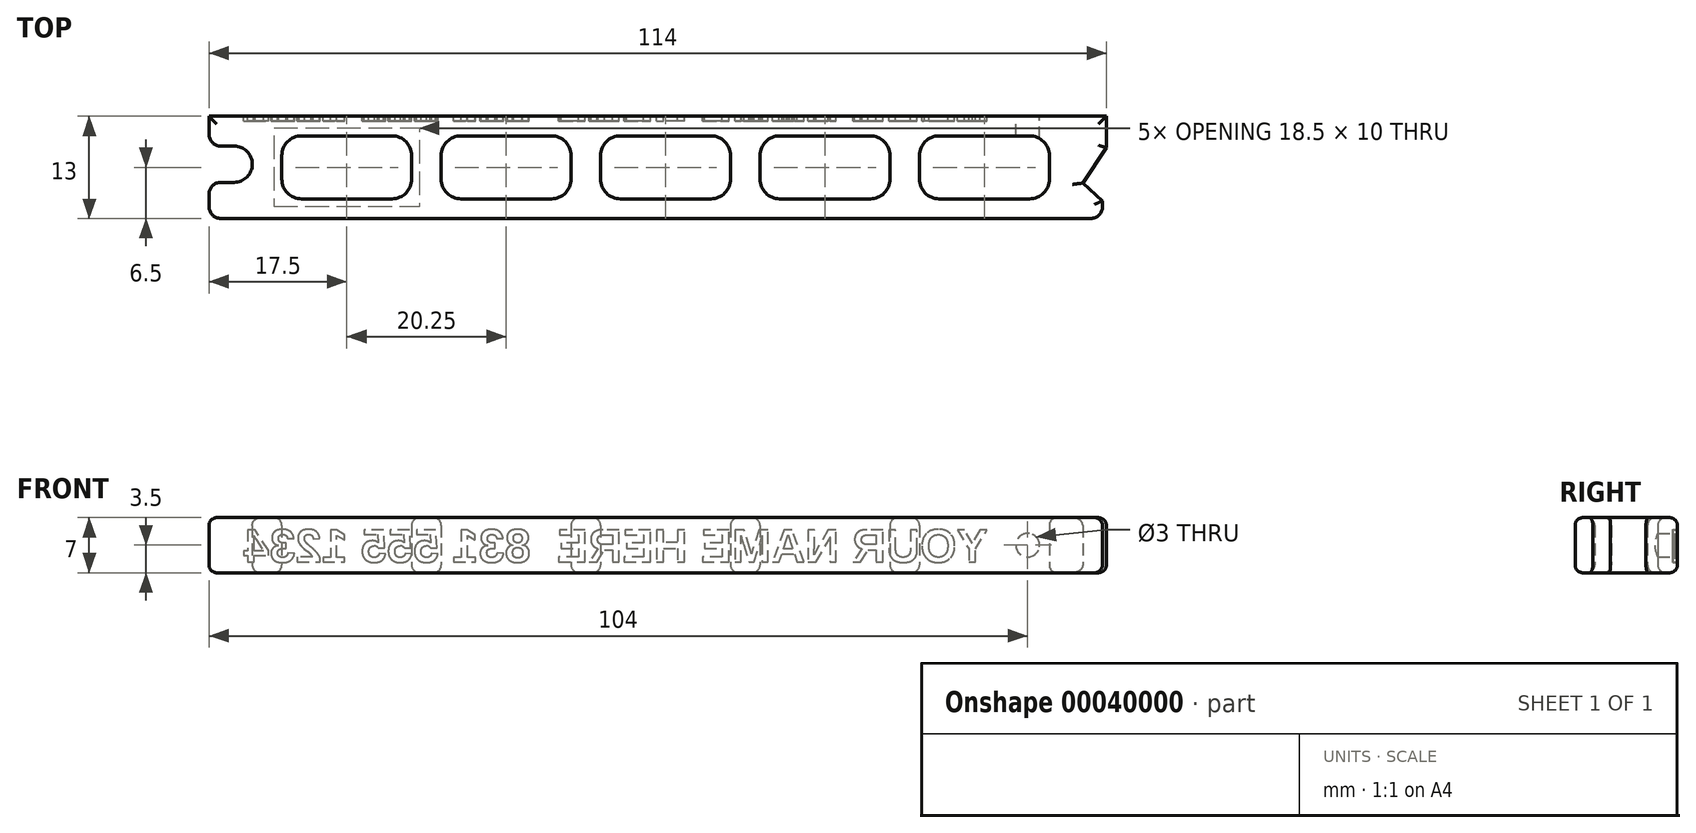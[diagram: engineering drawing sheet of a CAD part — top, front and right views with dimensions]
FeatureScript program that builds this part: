
annotation { "Feature Type Name" : "Feature", "Feature Type Description" : "" }
export const myFeature = defineFeature(function(context is Context, id is Id, definition is map)
    precondition{}
    {
        {
            var Q0;
            Q0=qCreatedBy(makeId("Top.planeOp"),FACE);
            var sketch = newSketch(context, id + "F0", { "sketchPlane" : qUnion([Q0])});
            skLineSegment(sketch, "E0.bottom", {"start": v(1.5, 0) * mm, "end": v(112, 0) * mm});
            skLineSegment(sketch, "E0.top", {"start": v(0, 13) * mm, "end": v(114, 13) * mm});
            skLineSegment(sketch, "E1", {"start": v(0, 13) * mm, "end": v(0, 10.7) * mm});
            skLineSegment(sketch, "E2.bottom", {"start": v(1.5, 4.6) * mm, "end": v(3.2, 4.6) * mm});
            skLineSegment(sketch, "E2.top", {"start": v(1.5, 9.2) * mm, "end": v(3.2, 9.2) * mm});
            skArc(sketch, "E3", {"start": v(3.2, 4.6) * mm, "mid": v(5.5, 6.9) * mm, "end": v(3.2, 9.2) * mm});
            skLineSegment(sketch, "E4.trimOffspring", {"start": v(0, 3.1) * mm, "end": v(0, 1.5) * mm});
            skLineSegment(sketch, "E5", {"start": v(0, 9.2) * mm, "end": v(0, 4.6) * mm, "construction": true});
            skLineSegment(sketch, "E6", {"start": v(0, 6.9) * mm, "end": v(3.2, 6.9) * mm, "construction": true});
            skLineSegment(sketch, "E7", {"start": v(114, 13) * mm, "end": v(114, 9) * mm});
            skPoint(sketch, "E8.visualSharp", {"position": v(0, 0) * mm});
            skArc(sketch, "E8.filletArc", {"start": v(0, 1.5) * mm, "mid": v(0.44, 0.44) * mm, "end": v(1.5, 0) * mm});
            skPoint(sketch, "E9.visualSharp", {"position": v(0, 4.6) * mm});
            skArc(sketch, "E9.filletArc", {"start": v(1.5, 4.6) * mm, "mid": v(0.44, 4.16) * mm, "end": v(0, 3.1) * mm});
            skPoint(sketch, "E10.visualSharp", {"position": v(0, 9.2) * mm});
            skArc(sketch, "E10.filletArc", {"start": v(0, 10.7) * mm, "mid": v(0.44, 9.64) * mm, "end": v(1.5, 9.2) * mm});
            skPoint(sketch, "E11.visualSharp", {"position": v(114, 4.5) * mm});
            skLineSegment(sketch, "E12", {"start": v(114, 4.5) * mm, "end": v(111, 4.5) * mm, "construction": true});
            skLineSegment(sketch, "E13", {"start": v(114, 9) * mm, "end": v(111, 4.5) * mm});
            skLineSegment(sketch, "E14", {"start": v(113.5, 2.25) * mm, "end": v(111, 4.5) * mm});
            skArc(sketch, "E15", {"start": v(112, 0) * mm, "mid": v(113.06, 0.44) * mm, "end": v(113.5, 1.5) * mm});
            skLineSegment(sketch, "E16", {"start": v(112, 1.5) * mm, "end": v(114.8, 1.5) * mm, "construction": true});
            skLineSegment(sketch, "E17", {"start": v(113.5, 2.25) * mm, "end": v(113.5, 1.5) * mm});
            skSolve(sketch);
        }
        {
            var Q0;
            Q0=makeQuery(id+"F0.imprint","IMPRINT",FACE,{"disambiguationData":[TD([[makeQuery(id+"F0.imprint","IMPRINT",EDGE,{"derivedFrom":sQuery(id+"F0.wireOp",EDGE,"E0.bottom")}),1.0]])]});
            extrude(context, id + "F1", {"entities" : qUnion([Q0]), "depth" : 7 * mm});
        }
        {
            var Q0;
            Q0=makeQuery(id+"F1.opExtrude","CAP_FACE",FACE,{"disambiguationData":[OSD([sQuery(id+"F0.wireOp",EDGE,"E0.bottom"),sQuery(id+"F0.wireOp",EDGE,"E0.top"),sQuery(id+"F0.wireOp",EDGE,"E1"),sQuery(id+"F0.wireOp",EDGE,"E2.bottom"),sQuery(id+"F0.wireOp",EDGE,"E2.top"),sQuery(id+"F0.wireOp",EDGE,"E3"),sQuery(id+"F0.wireOp",EDGE,"E4.trimOffspring"),sQuery(id+"F0.wireOp",EDGE,"E7"),sQuery(id+"F0.wireOp",EDGE,"c30ca287-96d4-4dfe-8688-3bdeec023004"),sQuery(id+"F0.wireOp",EDGE,"f645941c-dc99-4dda-a8e2-c4b280260802"),sQuery(id+"F0.wireOp",EDGE,"a89c6d0d-95b4-4aa5-8d05-a083aa38cfd4")])],"isStart":true});
            var sketch = newSketch(context, id + "F2", { "sketchPlane" : qUnion([Q0])});
            skLineSegment(sketch, "E18.bottom", {"start": v(104.25, -2.5) * mm, "end": v(92.75, -2.5) * mm});
            skLineSegment(sketch, "E18.top", {"start": v(104.25, -10.5) * mm, "end": v(92.75, -10.5) * mm});
            skLineSegment(sketch, "E18.left", {"start": v(106.75, -5) * mm, "end": v(106.75, -8) * mm});
            skLineSegment(sketch, "E18.right", {"start": v(90.25, -5) * mm, "end": v(90.25, -8) * mm});
            skLineSegment(sketch, "E19", {"start": v(106.75, -10.5) * mm, "end": v(106.75, -13) * mm, "construction": true});
            skLineSegment(sketch, "E20", {"start": v(106.75, -2.5) * mm, "end": v(106.75, 0) * mm, "construction": true});
            skPoint(sketch, "E21.visualSharp", {"position": v(90.25, -10.5) * mm});
            skArc(sketch, "E21.filletArc", {"start": v(90.25, -8) * mm, "mid": v(90.98, -9.77) * mm, "end": v(92.75, -10.5) * mm});
            skPoint(sketch, "E22.visualSharp", {"position": v(90.25, -2.5) * mm});
            skArc(sketch, "E22.filletArc", {"start": v(92.75, -2.5) * mm, "mid": v(90.98, -3.23) * mm, "end": v(90.25, -5) * mm});
            skPoint(sketch, "E23.visualSharp", {"position": v(106.75, -2.5) * mm});
            skArc(sketch, "E23.filletArc", {"start": v(106.75, -5) * mm, "mid": v(106.02, -3.23) * mm, "end": v(104.25, -2.5) * mm});
            skPoint(sketch, "E24.visualSharp", {"position": v(106.75, -10.5) * mm});
            skArc(sketch, "E24.filletArc", {"start": v(104.25, -10.5) * mm, "mid": v(106.02, -9.77) * mm, "end": v(106.75, -8) * mm});
            skLineSegment(sketch, "E25.1.0.0", {"start": v(84, -2.5) * mm, "end": v(72.5, -2.5) * mm});
            skPoint(sketch, "E25.1.0.1", {"position": v(86.5, -2.5) * mm});
            skLineSegment(sketch, "E25.1.0.2", {"start": v(84, -10.5) * mm, "end": v(72.5, -10.5) * mm});
            skPoint(sketch, "E25.1.0.3", {"position": v(86.5, -10.5) * mm});
            skLineSegment(sketch, "E25.1.0.4", {"start": v(70, -5) * mm, "end": v(70, -8) * mm});
            skLineSegment(sketch, "E25.1.0.5", {"start": v(86.5, -5) * mm, "end": v(86.5, -8) * mm});
            skPoint(sketch, "E25.1.0.6", {"position": v(70, -2.5) * mm});
            skPoint(sketch, "E25.1.0.7", {"position": v(70, -10.5) * mm});
            skArc(sketch, "E25.1.0.8", {"start": v(72.5, -2.5) * mm, "mid": v(70.73, -3.23) * mm, "end": v(70, -5) * mm});
            skArc(sketch, "E25.1.0.9", {"start": v(70, -8) * mm, "mid": v(70.73, -9.77) * mm, "end": v(72.5, -10.5) * mm});
            skArc(sketch, "E25.1.0.10", {"start": v(86.5, -5) * mm, "mid": v(85.77, -3.23) * mm, "end": v(84, -2.5) * mm});
            skArc(sketch, "E25.1.0.11", {"start": v(84, -10.5) * mm, "mid": v(85.77, -9.77) * mm, "end": v(86.5, -8) * mm});
            skLineSegment(sketch, "E25.2.0.0", {"start": v(63.75, -2.5) * mm, "end": v(52.25, -2.5) * mm});
            skPoint(sketch, "E25.2.0.1", {"position": v(66.25, -2.5) * mm});
            skLineSegment(sketch, "E25.2.0.2", {"start": v(63.75, -10.5) * mm, "end": v(52.25, -10.5) * mm});
            skPoint(sketch, "E25.2.0.3", {"position": v(66.25, -10.5) * mm});
            skLineSegment(sketch, "E25.2.0.4", {"start": v(49.75, -5) * mm, "end": v(49.75, -8) * mm});
            skLineSegment(sketch, "E25.2.0.5", {"start": v(66.25, -5) * mm, "end": v(66.25, -8) * mm});
            skPoint(sketch, "E25.2.0.6", {"position": v(49.75, -2.5) * mm});
            skPoint(sketch, "E25.2.0.7", {"position": v(49.75, -10.5) * mm});
            skArc(sketch, "E25.2.0.8", {"start": v(52.25, -2.5) * mm, "mid": v(50.48, -3.23) * mm, "end": v(49.75, -5) * mm});
            skArc(sketch, "E25.2.0.9", {"start": v(49.75, -8) * mm, "mid": v(50.48, -9.77) * mm, "end": v(52.25, -10.5) * mm});
            skArc(sketch, "E25.2.0.10", {"start": v(66.25, -5) * mm, "mid": v(65.52, -3.23) * mm, "end": v(63.75, -2.5) * mm});
            skArc(sketch, "E25.2.0.11", {"start": v(63.75, -10.5) * mm, "mid": v(65.52, -9.77) * mm, "end": v(66.25, -8) * mm});
            skLineSegment(sketch, "E25.3.0.0", {"start": v(43.5, -2.5) * mm, "end": v(32, -2.5) * mm});
            skPoint(sketch, "E25.3.0.1", {"position": v(46, -2.5) * mm});
            skLineSegment(sketch, "E25.3.0.2", {"start": v(43.5, -10.5) * mm, "end": v(32, -10.5) * mm});
            skPoint(sketch, "E25.3.0.3", {"position": v(46, -10.5) * mm});
            skLineSegment(sketch, "E25.3.0.4", {"start": v(29.5, -5) * mm, "end": v(29.5, -8) * mm});
            skLineSegment(sketch, "E25.3.0.5", {"start": v(46, -5) * mm, "end": v(46, -8) * mm});
            skPoint(sketch, "E25.3.0.6", {"position": v(29.5, -2.5) * mm});
            skPoint(sketch, "E25.3.0.7", {"position": v(29.5, -10.5) * mm});
            skArc(sketch, "E25.3.0.8", {"start": v(32, -2.5) * mm, "mid": v(30.23, -3.23) * mm, "end": v(29.5, -5) * mm});
            skArc(sketch, "E25.3.0.9", {"start": v(29.5, -8) * mm, "mid": v(30.23, -9.77) * mm, "end": v(32, -10.5) * mm});
            skArc(sketch, "E25.3.0.10", {"start": v(46, -5) * mm, "mid": v(45.27, -3.23) * mm, "end": v(43.5, -2.5) * mm});
            skArc(sketch, "E25.3.0.11", {"start": v(43.5, -10.5) * mm, "mid": v(45.27, -9.77) * mm, "end": v(46, -8) * mm});
            skLineSegment(sketch, "E25.4.0.0", {"start": v(23.25, -2.5) * mm, "end": v(11.75, -2.5) * mm});
            skPoint(sketch, "E25.4.0.1", {"position": v(25.75, -2.5) * mm});
            skLineSegment(sketch, "E25.4.0.2", {"start": v(23.25, -10.5) * mm, "end": v(11.75, -10.5) * mm});
            skPoint(sketch, "E25.4.0.3", {"position": v(25.75, -10.5) * mm});
            skLineSegment(sketch, "E25.4.0.4", {"start": v(9.25, -5) * mm, "end": v(9.25, -8) * mm});
            skLineSegment(sketch, "E25.4.0.5", {"start": v(25.75, -5) * mm, "end": v(25.75, -8) * mm});
            skPoint(sketch, "E25.4.0.6", {"position": v(9.25, -2.5) * mm});
            skPoint(sketch, "E25.4.0.7", {"position": v(9.25, -10.5) * mm});
            skArc(sketch, "E25.4.0.8", {"start": v(11.75, -2.5) * mm, "mid": v(9.98, -3.23) * mm, "end": v(9.25, -5) * mm});
            skArc(sketch, "E25.4.0.9", {"start": v(9.25, -8) * mm, "mid": v(9.98, -9.77) * mm, "end": v(11.75, -10.5) * mm});
            skArc(sketch, "E25.4.0.10", {"start": v(25.75, -5) * mm, "mid": v(25.02, -3.23) * mm, "end": v(23.25, -2.5) * mm});
            skArc(sketch, "E25.4.0.11", {"start": v(23.25, -10.5) * mm, "mid": v(25.02, -9.77) * mm, "end": v(25.75, -8) * mm});
            skLineSegment(sketch, "E25.direction1", {"start": v(92.75, -2.5) * mm, "end": v(72.5, -2.5) * mm, "construction": true});
            skSolve(sketch);
        }
        {
            var Q0;
            Q0=qSketchRegion(id+"F2",true);
            extrude(context, id + "F3", {"entities" : qUnion([Q0]), "operationType" : NewBodyOperationType.REMOVE, "endBound" : BoundingType.THROUGH_ALL, "oppositeDirection" : true, "depth" : 13.73 * mm});
        }
        {
            var Q0;
            Q0=makeQuery(id+"F1.opExtrude","CAP_FACE",FACE,{"disambiguationData":[OSD([sQuery(id+"F0.wireOp",EDGE,"E0.bottom"),sQuery(id+"F0.wireOp",EDGE,"E0.top"),sQuery(id+"F0.wireOp",EDGE,"E1"),sQuery(id+"F0.wireOp",EDGE,"E2.bottom"),sQuery(id+"F0.wireOp",EDGE,"E2.top"),sQuery(id+"F0.wireOp",EDGE,"E3"),sQuery(id+"F0.wireOp",EDGE,"E4.trimOffspring"),sQuery(id+"F0.wireOp",EDGE,"E7"),sQuery(id+"F0.wireOp",EDGE,"a89c6d0d-95b4-4aa5-8d05-a083aa38cfd4"),sQuery(id+"F0.wireOp",EDGE,"843786d9-8344-4bf4-b63c-bd20b21d23d6.filletArc"),sQuery(id+"F0.wireOp",EDGE,"E8.filletArc"),sQuery(id+"F0.wireOp",EDGE,"E9.filletArc"),sQuery(id+"F0.wireOp",EDGE,"E10.filletArc"),sQuery(id+"F0.wireOp",EDGE,"E13"),sQuery(id+"F0.wireOp",EDGE,"34148787-0765-4789-8ede-2cb2b04cca70")])],"isStart":true});
            var Q1;
            Q1=makeQuery(id+"F1.opExtrude","CAP_FACE",FACE,{"disambiguationData":[OSD([sQuery(id+"F0.wireOp",EDGE,"E0.bottom"),sQuery(id+"F0.wireOp",EDGE,"E0.top"),sQuery(id+"F0.wireOp",EDGE,"E1"),sQuery(id+"F0.wireOp",EDGE,"E2.bottom"),sQuery(id+"F0.wireOp",EDGE,"E2.top"),sQuery(id+"F0.wireOp",EDGE,"E3"),sQuery(id+"F0.wireOp",EDGE,"E4.trimOffspring"),sQuery(id+"F0.wireOp",EDGE,"E7"),sQuery(id+"F0.wireOp",EDGE,"a89c6d0d-95b4-4aa5-8d05-a083aa38cfd4"),sQuery(id+"F0.wireOp",EDGE,"843786d9-8344-4bf4-b63c-bd20b21d23d6.filletArc"),sQuery(id+"F0.wireOp",EDGE,"E8.filletArc"),sQuery(id+"F0.wireOp",EDGE,"E9.filletArc"),sQuery(id+"F0.wireOp",EDGE,"E10.filletArc"),sQuery(id+"F0.wireOp",EDGE,"E13"),sQuery(id+"F0.wireOp",EDGE,"34148787-0765-4789-8ede-2cb2b04cca70")])],"isStart":false});
            fillet(context, id + "F4", {"entities" : qUnion([Q0, Q1]), "radius" : 1 * mm, "allowEdgeOverflow" : false});
        }
        {
            var Q0;
            Q0=makeQuery(id+"F1.opExtrude","SWEPT_FACE",FACE,{"disambiguationData":[OSD([sQuery(id+"F0.wireOp",EDGE,"E0.top")])]});
            var sketch = newSketch(context, id + "F5", { "sketchPlane" : qUnion([Q0])});
            skLineSegment(sketch, "E26", {"start": v(-104, 1) * mm, "end": v(-104, 6) * mm, "construction": true});
            skCircle(sketch, "E27", {"center": v(-104, 3.5) * mm, "radius": 1.5 * mm});
            skSolve(sketch);
        }
        {
            var Q0;
            Q0=makeQuery(id+"F5.imprint","IMPRINT",FACE,{"disambiguationData":[TD([[makeQuery(id+"F5.imprint","IMPRINT",EDGE,{"derivedFrom":sQuery(id+"F5.wireOp",EDGE,"E27")}),1.0]])]});
            extrude(context, id + "F6", {"entities" : qUnion([Q0]), "operationType" : NewBodyOperationType.REMOVE, "endBound" : BoundingType.UP_TO_NEXT, "oppositeDirection" : true, "depth" : 25 * mm});
        }
        {
            var Q0;
            Q0=makeQuery(id+"F1.opExtrude","SWEPT_FACE",FACE,{"disambiguationData":[OSD([sQuery(id+"F0.wireOp",EDGE,"E0.top")])]});
            var sketch = newSketch(context, id + "F7", { "sketchPlane" : qUnion([Q0])});
            skText(sketch, "E28", { "text": "YOUR NAME HERE  831 555 1234", "fontName": "Arimo-Bold.ttf"});
            skLineSegment(sketch, "E29", {"start": v(-98.95, 5.65) * mm, "end": v(-98.95, 6) * mm, "construction": true});
            skLineSegment(sketch, "E30", {"start": v(-98.95, 1.35) * mm, "end": v(-98.95, 1) * mm, "construction": true});
            const initialGuessF7  = {"E28": [-0.09895, 0.00135, 1, 0, 0.0043]};
            skSetInitialGuess(sketch, initialGuessF7);
            skSolve(sketch);
        }
        {
            var Q0;
            Q0 = qSketchRegion(id + "F7", true);
            extrude(context, id + "F8", {"entities" : qUnion([Q0]), "operationType" : NewBodyOperationType.REMOVE, "oppositeDirection" : true, "depth" : .6 * mm});
        }
    });
